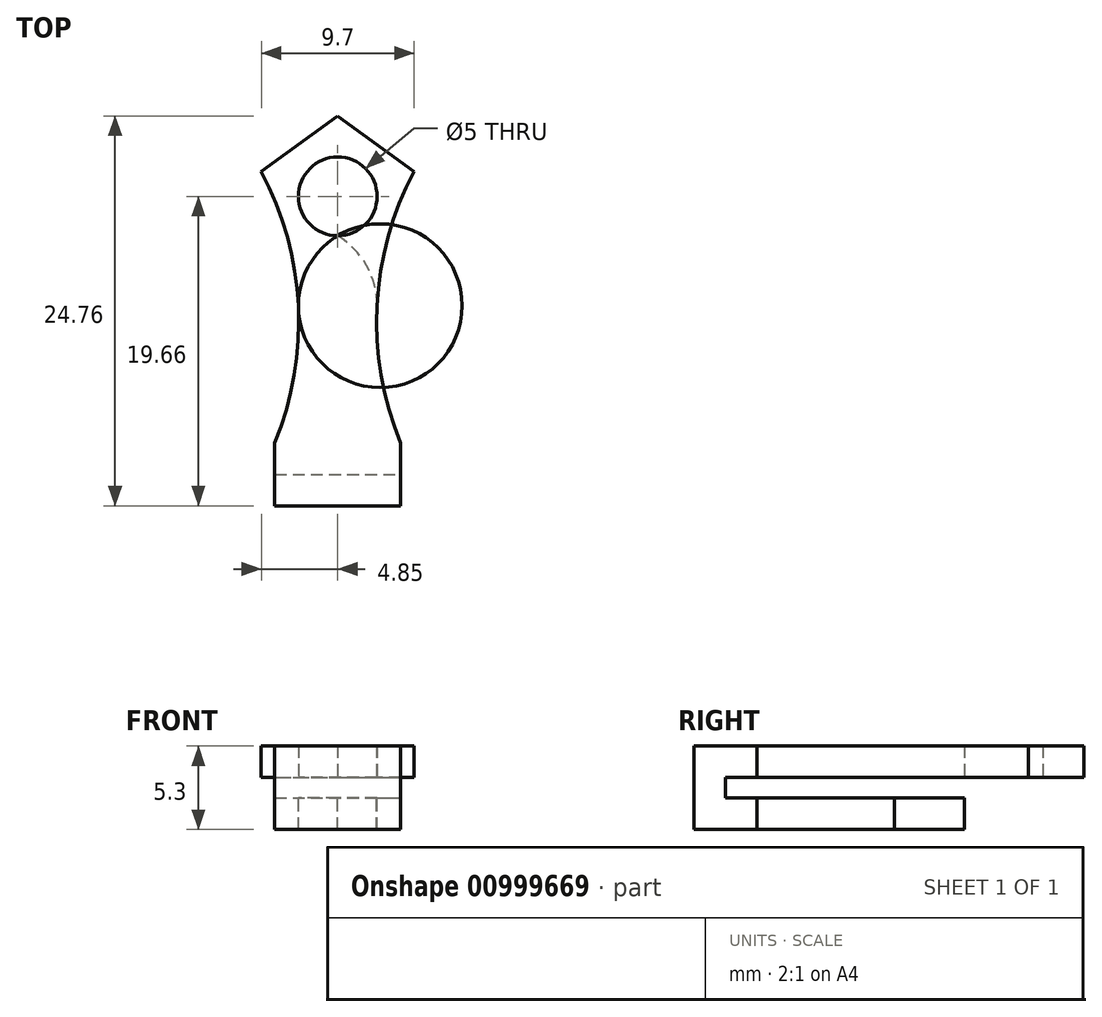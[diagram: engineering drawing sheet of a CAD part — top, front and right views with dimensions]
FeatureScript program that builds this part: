
annotation { "Feature Type Name" : "Feature", "Feature Type Description" : "" }
export const myFeature = defineFeature(function(context is Context, id is Id, definition is map)
    precondition{}
    {
        {
            var Q0;
            Q0=qCreatedBy(makeId("Top.planeOp"),FACE);
            var sketch = newSketch(context, id + "F0", { "sketchPlane" : qUnion([Q0])});
            skLineSegment(sketch, "E0", {"start": v(0, 0) * mm, "end": v(0, 19.66) * mm, "construction": true});
            skCircle(sketch, "E1", {"center": v(0, 19.66) * mm, "radius": 2.5 * mm});
            skCircle(sketch, "E2.cCircle", {"center": v(0, 19.66) * mm, "radius": 4.13 * mm, "construction": true});
            skLineSegment(sketch, "E2.0", {"start": v(3, 15.53) * mm, "end": v(-3, 15.53) * mm, "construction": true});
            skLineSegment(sketch, "E2.1", {"start": v(-3, 15.53) * mm, "end": v(-4.85, 21.24) * mm, "construction": true});
            skLineSegment(sketch, "E2.2", {"start": v(-4.85, 21.24) * mm, "end": v(0, 24.76) * mm});
            skLineSegment(sketch, "E2.3", {"start": v(0, 24.76) * mm, "end": v(4.85, 21.24) * mm});
            skLineSegment(sketch, "E2.4", {"start": v(4.85, 21.24) * mm, "end": v(3, 15.53) * mm, "construction": true});
            skPoint(sketch, "E2.0.midPoint", {"position": v(0, 15.53) * mm});
            skLineSegment(sketch, "E3.bottom", {"start": v(4, 0) * mm, "end": v(-4, 0) * mm});
            skLineSegment(sketch, "E3.top", {"start": v(4, 4) * mm, "end": v(-4, 4) * mm, "construction": true});
            skLineSegment(sketch, "E3.left", {"start": v(4, 0) * mm, "end": v(4, 4) * mm});
            skLineSegment(sketch, "E3.right", {"start": v(-4, 0) * mm, "end": v(-4, 4) * mm});
            skLineSegment(sketch, "E4", {"start": v(-4, 2) * mm, "end": v(4, 2) * mm});
            skLineSegment(sketch, "E5", {"start": v(-2.5, 12.71) * mm, "end": v(2.5, 12.71) * mm, "construction": true});
            skArc(sketch, "E6", {"start": v(-4, 4) * mm, "mid": v(-2.5, 12.71) * mm, "end": v(-4.85, 21.24) * mm});
            skArc(sketch, "E7", {"start": v(4.85, 21.24) * mm, "mid": v(2.5, 12.71) * mm, "end": v(4, 4) * mm});
            skPoint(sketch, "E8", {"position": v(0, 12.71) * mm});
            skLineSegment(sketch, "E9", {"start": v(-4, 4) * mm, "end": v(-4, 19.66) * mm});
            skLineSegment(sketch, "E10", {"start": v(-4, 19.66) * mm, "end": v(4, 19.66) * mm});
            skLineSegment(sketch, "E11", {"start": v(4, 19.66) * mm, "end": v(4, 4) * mm});
            skLineSegment(sketch, "E12", {"start": v(-2.5, 12.71) * mm, "end": v(-2.5, 19.66) * mm});
            skLineSegment(sketch, "E13", {"start": v(2.5, 12.71) * mm, "end": v(2.5, 19.66) * mm});
            skArc(sketch, "E14", {"start": v(0, 17.16) * mm, "mid": v(-1.83, 15.26) * mm, "end": v(-2.5, 12.71) * mm});
            skArc(sketch, "E15", {"start": v(2.5, 12.71) * mm, "mid": v(1.83, 15.26) * mm, "end": v(0, 17.16) * mm});
            skSolve(sketch);
        }
        {
            var Q0;
            {var subQ1=sQuery(id+"F0.wireOp",EDGE,"E2.2");Q0=makeQuery(id+"F0.imprint","IMPRINT",FACE,{"disambiguationData":[TD([[makeQuery(id+"F0.imprint","IMPRINT",EDGE,{"derivedFrom":subQ1}),-1.0]])]});}
            var Q1;
            {var subQ0=sQuery(id+"F0.wireOp",EDGE,"E4");Q1=makeQuery(id+"F0.imprint","IMPRINT",FACE,{"disambiguationData":[TD([[makeQuery(id+"F0.imprint","IMPRINT",EDGE,{"derivedFrom":subQ0}),1.0]])]});}
            var Q2;
            {var subQ0=sQuery(id+"F0.wireOp",EDGE,"E3.bottom");Q2=makeQuery(id+"F0.imprint","IMPRINT",FACE,{"disambiguationData":[TD([[makeQuery(id+"F0.imprint","IMPRINT",EDGE,{"derivedFrom":subQ0}),-1.0]])]});}
            var Q3;
            {var subQ4=sQuery(id+"F0.wireOp",EDGE,"E12");Q3=makeQuery(id+"F0.imprint","IMPRINT",FACE,{"disambiguationData":[TD([[makeQuery(id+"F0.imprint","IMPRINT",EDGE,{"derivedFrom":subQ4}),-1.0]])]});}
            var Q4;
            {var subQ4=sQuery(id+"F0.wireOp",EDGE,"E13");Q4=makeQuery(id+"F0.imprint","IMPRINT",FACE,{"disambiguationData":[TD([[makeQuery(id+"F0.imprint","IMPRINT",EDGE,{"derivedFrom":subQ4}),1.0]])]});}
            var Q5;
            {var subQ0=sQuery(id+"F0.wireOp",EDGE,"E10");var subQ7=sQuery(id+"F0.wireOp",EDGE,"E1");var subQ8=makeQuery(id+"F0.imprint","INTERSECT",VERTEX,{"disambiguationData":[OD(0.0)],"derivedFrom":[subQ7,subQ0]});Q5=makeQuery(id+"F0.imprint","IMPRINT",FACE,{"disambiguationData":[TD([[makeQuery(id+"F0.imprint","IMPRINT",EDGE,{"disambiguationData":[TD([[subQ8,-1.0]])],"derivedFrom":subQ7}),-1.0]])]});}
            var Q6;
            {var subQ1=sQuery(id+"F0.wireOp",EDGE,"E10");var subQ5=sQuery(id+"F0.wireOp",EDGE,"E1");var subQ6=makeQuery(id+"F0.imprint","INTERSECT",VERTEX,{"disambiguationData":[OD(1.0)],"derivedFrom":[subQ5,subQ1]});Q6=makeQuery(id+"F0.imprint","IMPRINT",FACE,{"disambiguationData":[TD([[makeQuery(id+"F0.imprint","IMPRINT",EDGE,{"disambiguationData":[TD([[subQ6,1.0]])],"derivedFrom":subQ5}),-1.0]])]});}
            var Q7;
            {var subQ0=sQuery(id+"F0.wireOp",EDGE,"E12");Q7=makeQuery(id+"F0.imprint","IMPRINT",FACE,{"disambiguationData":[TD([[makeQuery(id+"F0.imprint","IMPRINT",EDGE,{"derivedFrom":subQ0}),1.0]])]});}
            var Q8;
            {var subQ0=sQuery(id+"F0.wireOp",EDGE,"E13");Q8=makeQuery(id+"F0.imprint","IMPRINT",FACE,{"disambiguationData":[TD([[makeQuery(id+"F0.imprint","IMPRINT",EDGE,{"derivedFrom":subQ0}),-1.0]])]});}
            extrude(context, id + "F1", {"entities" : qUnion([Q0, Q1, Q2, Q3, Q4, Q5, Q6, Q7, Q8]), "depth" : 2 * mm, "offsetDistance" : 25 * mm});
        }
        {
            var Q0;
            {var subQ0=sQuery(id+"F0.wireOp",EDGE,"E3.bottom");Q0=makeQuery(id+"F0.imprint","IMPRINT",FACE,{"disambiguationData":[TD([[makeQuery(id+"F0.imprint","IMPRINT",EDGE,{"derivedFrom":subQ0}),-1.0]])]});}
            extrude(context, id + "F2", {"entities" : qUnion([Q0]), "operationType" : NewBodyOperationType.ADD, "oppositeDirection" : true, "depth" : 1.3 * mm, "offsetDistance" : 25 * mm});
        }
        {
            var Q0;
            {var subQ0=sQuery(id+"F0.wireOp",EDGE,"E4");Q0=makeQuery(id+"F0.imprint","IMPRINT",FACE,{"disambiguationData":[TD([[makeQuery(id+"F0.imprint","IMPRINT",EDGE,{"derivedFrom":subQ0}),1.0]])]});}
            var Q1;
            {var subQ0=sQuery(id+"F0.wireOp",EDGE,"E3.bottom");Q1=makeQuery(id+"F0.imprint","IMPRINT",FACE,{"disambiguationData":[TD([[makeQuery(id+"F0.imprint","IMPRINT",EDGE,{"derivedFrom":subQ0}),-1.0]])]});}
            extrude(context, id + "F3", {"entities" : qUnion([Q0, Q1]), "operationType" : NewBodyOperationType.ADD, "oppositeDirection" : true, "depth" : 3.3 * mm, "offsetDistance" : 25 * mm, "hasSecondDirection" : true, "secondDirectionOppositeDirection" : true, "secondDirectionDepth" : 1.3 * mm});
        }
    });
